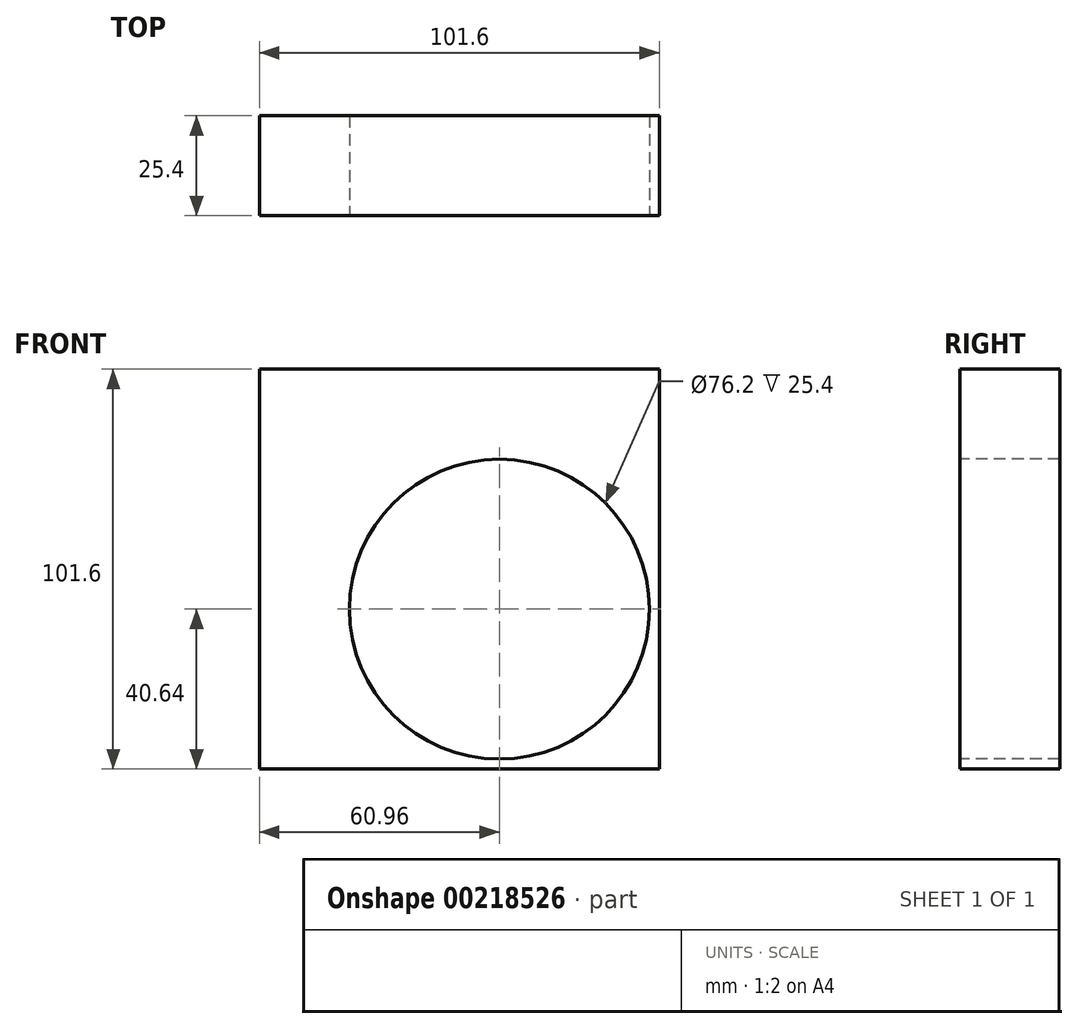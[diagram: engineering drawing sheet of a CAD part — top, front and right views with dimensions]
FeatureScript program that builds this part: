
annotation { "Feature Type Name" : "Feature", "Feature Type Description" : "" }
export const myFeature = defineFeature(function(context is Context, id is Id, definition is map)
    precondition{}
    {
        {
            var Q0;
            Q0=qCreatedBy(makeId("Front.planeOp"),FACE);
            var sketch = newSketch(context, id + "F0", { "sketchPlane" : qUnion([Q0])});
            skLineSegment(sketch, "E0.bottom", {"start": v(-50.8, 50.8) * mm, "end": v(50.8, 50.8) * mm});
            skLineSegment(sketch, "E0.top", {"start": v(-50.8, -50.8) * mm, "end": v(50.8, -50.8) * mm});
            skLineSegment(sketch, "E0.left", {"start": v(-50.8, 50.8) * mm, "end": v(-50.8, -50.8) * mm});
            skLineSegment(sketch, "E0.right", {"start": v(50.8, 50.8) * mm, "end": v(50.8, -50.8) * mm});
            skSolve(sketch);
        }
        {
            var Q0;
            Q0 = qSketchRegion(id + "F0", true);
            extrude(context, id + "F1", {"entities" : qUnion([Q0]), "depth" : 25.4 * mm});
        }
        {
            var Q0;
            Q0=makeQuery(id+"F1.opExtrude","CAP_FACE",FACE,{"disambiguationData":[OSD([sQuery(id+"F0.wireOp",EDGE,"E0.bottom"),sQuery(id+"F0.wireOp",EDGE,"E0.top"),sQuery(id+"F0.wireOp",EDGE,"E0.left"),sQuery(id+"F0.wireOp",EDGE,"E0.right")])],"isStart":false});
            var sketch = newSketch(context, id + "F2", { "sketchPlane" : qUnion([Q0])});
            skCircle(sketch, "E1", {"center": v(10.16, -10.16) * mm, "radius": 38.1 * mm});
            skSolve(sketch);
        }
        {
            var Q0;
            Q0=makeQuery(id+"F2.imprint","IMPRINT",FACE,{"disambiguationData":[TD([[makeQuery(id+"F2.imprint","IMPRINT",EDGE,{"derivedFrom":sQuery(id+"F2.wireOp",EDGE,"gI4ZZPZA-TRXo-dIBC-nXic-hExinUQA6CdL")}),1.0]])]});
            var Q1;
            Q1=makeQuery(id+"F2.imprint","IMPRINT",FACE,{"disambiguationData":[TD([[makeQuery(id+"F2.imprint","IMPRINT",EDGE,{"derivedFrom":sQuery(id+"F2.wireOp",EDGE,"E1")}),1.0]])]});
            extrude(context, id + "F3", {"entities" : qUnion([Q0, Q1]), "operationType" : NewBodyOperationType.REMOVE, "oppositeDirection" : true, "depth" : 25.4 * mm});
        }
    });
